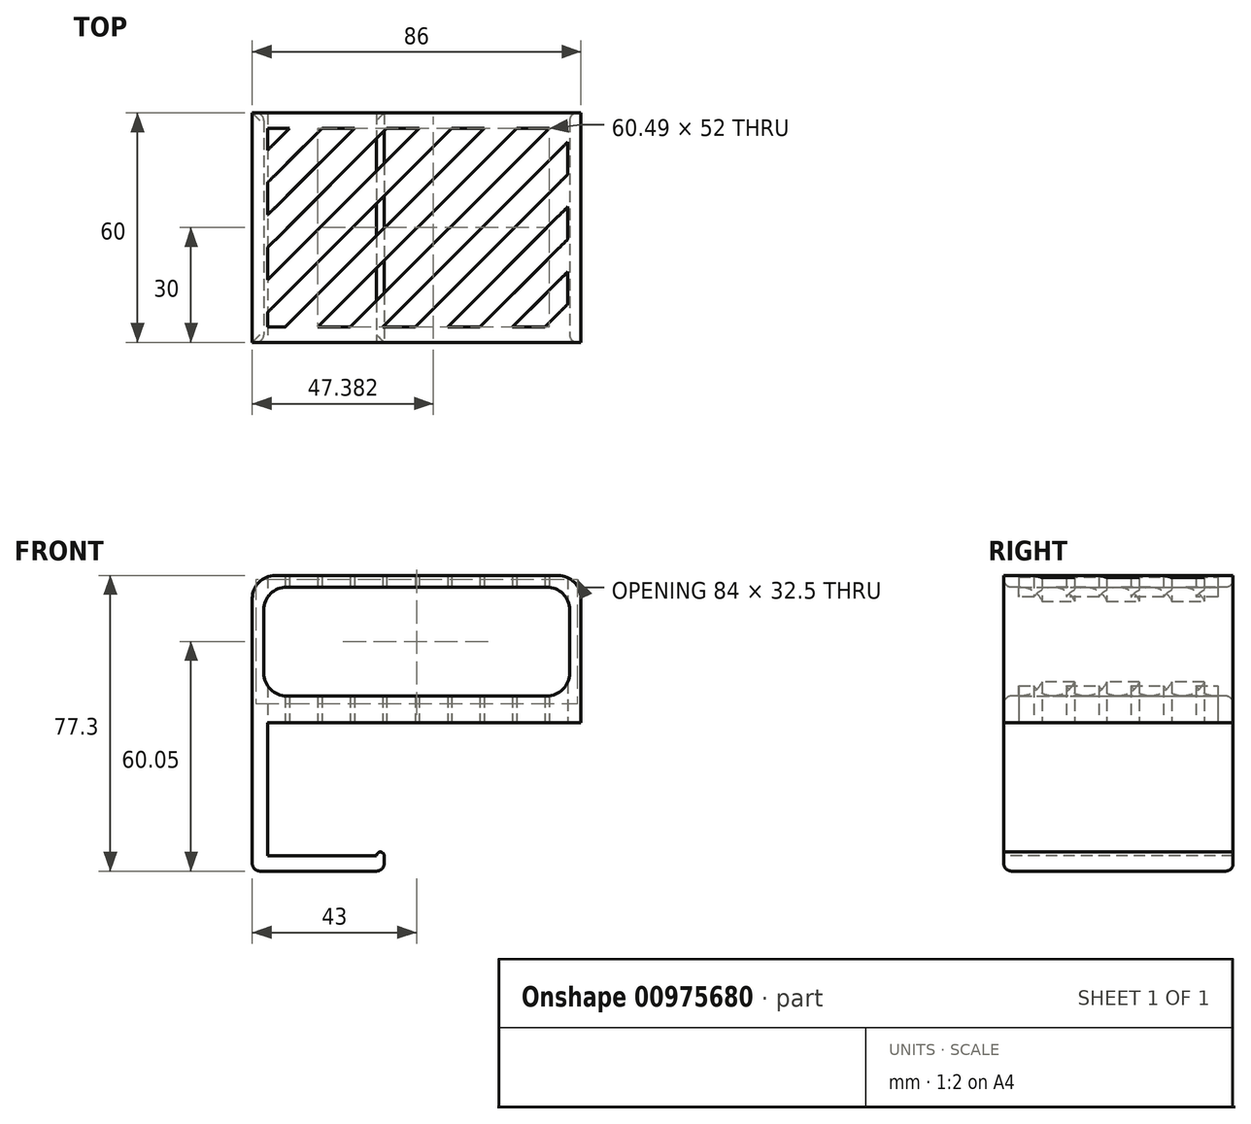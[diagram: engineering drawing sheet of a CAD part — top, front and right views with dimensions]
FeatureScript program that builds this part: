
annotation { "Feature Type Name" : "Feature", "Feature Type Description" : "" }
export const myFeature = defineFeature(function(context is Context, id is Id, definition is map)
    precondition{}
    {
        {
            var Q0;
            Q0=qCreatedBy(makeId("Front.planeOp"),FACE);
            var sketch = newSketch(context, id + "F0", { "sketchPlane" : qUnion([Q0])});
            skLineSegment(sketch, "E0.bottom", {"start": v(0, 51.9) * mm, "end": v(86, 51.9) * mm});
            skLineSegment(sketch, "E0.top", {"start": v(0, 17.4) * mm, "end": v(86, 17.4) * mm});
            skLineSegment(sketch, "E0.left", {"start": v(0, 51.9) * mm, "end": v(0, 17.4) * mm});
            skLineSegment(sketch, "E0.right", {"start": v(86, 51.9) * mm, "end": v(86, 17.4) * mm});
            skLineSegment(sketch, "E1.bottom", {"start": v(3, 48.9) * mm, "end": v(83, 48.9) * mm});
            skLineSegment(sketch, "E1.top", {"start": v(3, 20.4) * mm, "end": v(83, 20.4) * mm});
            skLineSegment(sketch, "E1.left", {"start": v(3, 48.9) * mm, "end": v(3, 20.4) * mm});
            skLineSegment(sketch, "E1.right", {"start": v(83, 48.9) * mm, "end": v(83, 20.4) * mm});
            skSolve(sketch);
        }
        {
            var Q0;
            Q0=qCreatedBy(makeId("Front.planeOp"),FACE);
            var sketch = newSketch(context, id + "F1", { "sketchPlane" : qUnion([Q0])});
            skLineSegment(sketch, "E2", {"start": v(0, 17.4) * mm, "end": v(0, -25.4) * mm});
            skPoint(sketch, "E3.0", {"position": v(86, 17.4) * mm});
            skLineSegment(sketch, "E4", {"start": v(0, 17.4) * mm, "end": v(86, 17.4) * mm});
            skLineSegment(sketch, "E5.0", {"start": v(4, 13.4) * mm, "end": v(86, 13.4) * mm});
            skLineSegment(sketch, "E6.0", {"start": v(0, -25.4) * mm, "end": v(34.5, -25.4) * mm});
            skLineSegment(sketch, "E7", {"start": v(4, -21.4) * mm, "end": v(34.5, -21.4) * mm});
            skLineSegment(sketch, "E8.bottom", {"start": v(34.5, -21.4) * mm, "end": v(32.5, -21.4) * mm});
            skLineSegment(sketch, "E8.top", {"start": v(34.5, -20.4) * mm, "end": v(32.5, -20.4) * mm});
            skLineSegment(sketch, "E8.left", {"start": v(34.5, -21.4) * mm, "end": v(34.5, -20.4) * mm});
            skLineSegment(sketch, "E8.right", {"start": v(32.5, -21.4) * mm, "end": v(32.5, -20.4) * mm});
            skLineSegment(sketch, "E9", {"start": v(63.21, 17.4) * mm, "end": v(-36.45, 17.4) * mm, "construction": true});
            skLineSegment(sketch, "E10", {"start": v(4, -21.4) * mm, "end": v(4, 13.4) * mm});
            skLineSegment(sketch, "E11", {"start": v(86, 13.4) * mm, "end": v(86, 17.4) * mm});
            skLineSegment(sketch, "E12", {"start": v(34.5, -25.4) * mm, "end": v(34.5, -21.4) * mm});
            skLineSegment(sketch, "E13", {"start": v(4, -4) * mm, "end": v(91.63, -4) * mm, "construction": true});
            skSolve(sketch);
        }
        {
            var Q0;
            Q0=makeQuery(id+"F0.imprint","IMPRINT",FACE,{"disambiguationData":[TD([[makeQuery(id+"F0.imprint","IMPRINT",EDGE,{"derivedFrom":sQuery(id+"F0.wireOp",EDGE,"E0.bottom")}),-1.0]])]});
            extrude(context, id + "F2", {"entities" : qUnion([Q0]), "oppositeDirection" : true, "depth" : 60 * mm, "offsetDistance" : 25 * mm});
        }
        {
            var Q0;
            Q0=qSketchRegion(id+"F1",true);
            var Q1;
            Q1=makeQuery(id+"F2.opExtrude","CAP_FACE",FACE,{"disambiguationData":[OSD([sQuery(id+"F0.wireOp",EDGE,"E0.bottom"),sQuery(id+"F0.wireOp",EDGE,"E0.top"),sQuery(id+"F0.wireOp",EDGE,"E0.left"),sQuery(id+"F0.wireOp",EDGE,"E0.right"),sQuery(id+"F0.wireOp",EDGE,"E1.bottom"),sQuery(id+"F0.wireOp",EDGE,"E1.top"),sQuery(id+"F0.wireOp",EDGE,"E1.left"),sQuery(id+"F0.wireOp",EDGE,"E1.right")])],"isStart":false});
            extrude(context, id + "F3", {"entities" : qUnion([Q0]), "operationType" : NewBodyOperationType.ADD, "endBound" : BoundingType.UP_TO_SURFACE, "oppositeDirection" : true, "depth" : 25 * mm, "endBoundEntityFace" : qUnion([Q1]), "offsetDistance" : 25 * mm});
        }
        {
            var Q0;
            Q0=qCreatedBy(makeId("Top.planeOp"),FACE);
            var sketch = newSketch(context, id + "F4", { "sketchPlane" : qUnion([Q0])});
            skLineSegment(sketch, "E14.0", {"start": v(0.04, 0) * mm, "end": v(86.54, 0) * mm, "construction": true});
            skLineSegment(sketch, "E15.0", {"start": v(86.54, 60) * mm, "end": v(86.54, 0) * mm, "construction": true});
            skLineSegment(sketch, "E16.0", {"start": v(86.54, 60) * mm, "end": v(0.04, 60) * mm, "construction": true});
            skLineSegment(sketch, "E17.0", {"start": v(0.04, 60) * mm, "end": v(0.04, 0) * mm, "construction": true});
            skLineSegment(sketch, "E18.0", {"start": v(82.54, 56) * mm, "end": v(82.54, 4) * mm});
            skLineSegment(sketch, "E18.1", {"start": v(82.54, 56) * mm, "end": v(4.04, 56) * mm});
            skLineSegment(sketch, "E18.2", {"start": v(4.04, 56) * mm, "end": v(4.04, 4) * mm});
            skLineSegment(sketch, "E18.3", {"start": v(4.04, 4) * mm, "end": v(82.54, 4) * mm});
            skLineSegment(sketch, "E19", {"start": v(76.54, 4) * mm, "end": v(76.54, 97.18) * mm, "construction": true});
            skLineSegment(sketch, "E20", {"start": v(76.54, 4) * mm, "end": v(82.54, 10) * mm});
            skLineSegment(sketch, "E21.0", {"start": v(68.05, 4) * mm, "end": v(82.54, 18.49) * mm});
            skLineSegment(sketch, "E22.0", {"start": v(59.57, 4) * mm, "end": v(82.54, 26.97) * mm});
            skLineSegment(sketch, "E23.0", {"start": v(51.08, 4) * mm, "end": v(82.54, 35.46) * mm});
            skLineSegment(sketch, "E24.0", {"start": v(42.6, 4) * mm, "end": v(82.54, 43.94) * mm});
            skLineSegment(sketch, "E25.0", {"start": v(34.1, 4) * mm, "end": v(82.54, 52.43) * mm});
            skLineSegment(sketch, "E26.0", {"start": v(25.62, 4) * mm, "end": v(77.62, 56) * mm});
            skLineSegment(sketch, "E27.0", {"start": v(17.14, 4) * mm, "end": v(69.14, 56) * mm});
            skLineSegment(sketch, "E28.0", {"start": v(8.65, 4) * mm, "end": v(60.65, 56) * mm});
            skLineSegment(sketch, "E29.0", {"start": v(4.04, 7.87) * mm, "end": v(52.17, 56) * mm});
            skLineSegment(sketch, "E30.0", {"start": v(5, 60) * mm, "end": v(5, 120) * mm});
            skLineSegment(sketch, "E31.0", {"start": v(4.04, 16.35) * mm, "end": v(43.68, 56) * mm});
            skLineSegment(sketch, "E32.0", {"start": v(4.04, 24.84) * mm, "end": v(35.2, 56) * mm});
            skLineSegment(sketch, "E33.0", {"start": v(4.04, 33.32) * mm, "end": v(26.71, 56) * mm});
            skLineSegment(sketch, "E34.0", {"start": v(4.04, 41.8) * mm, "end": v(18.23, 56) * mm});
            skLineSegment(sketch, "E35.0", {"start": v(4.04, 50.3) * mm, "end": v(9.74, 56) * mm});
            skSolve(sketch);
        }
        {
            var Q0;
            {var subQ0=sQuery(id+"F4.wireOp",EDGE,"E20");Q0=makeQuery(id+"F4.imprint","IMPRINT",FACE,{"disambiguationData":[TD([[makeQuery(id+"F4.imprint","IMPRINT",EDGE,{"derivedFrom":subQ0}),1.0]])]});}
            var Q1;
            {var subQ0=sQuery(id+"F4.wireOp",EDGE,"E22.0");Q1=makeQuery(id+"F4.imprint","IMPRINT",FACE,{"disambiguationData":[TD([[makeQuery(id+"F4.imprint","IMPRINT",EDGE,{"derivedFrom":subQ0}),1.0]])]});}
            var Q2;
            {var subQ0=sQuery(id+"F4.wireOp",EDGE,"E24.0");Q2=makeQuery(id+"F4.imprint","IMPRINT",FACE,{"disambiguationData":[TD([[makeQuery(id+"F4.imprint","IMPRINT",EDGE,{"derivedFrom":subQ0}),1.0]])]});}
            var Q3;
            {var subQ0=sQuery(id+"F4.wireOp",EDGE,"E26.0");var subQ1=sQuery(id+"F4.wireOp",EDGE,"E18.1");var subQ2=makeQuery(id+"F4.imprint","INTERSECT",VERTEX,{"derivedFrom":[subQ1,subQ0]});Q3=makeQuery(id+"F4.imprint","IMPRINT",FACE,{"disambiguationData":[TD([[makeQuery(id+"F4.imprint","IMPRINT",EDGE,{"disambiguationData":[TD([[subQ2,-1.0]])],"derivedFrom":subQ1}),1.0]])]});}
            var Q4;
            {var subQ0=sQuery(id+"F4.wireOp",EDGE,"E26.0");var subQ1=sQuery(id+"F4.wireOp",EDGE,"E18.3");var subQ2=makeQuery(id+"F4.imprint","INTERSECT",VERTEX,{"derivedFrom":[subQ1,subQ0]});Q4=makeQuery(id+"F4.imprint","IMPRINT",FACE,{"disambiguationData":[TD([[makeQuery(id+"F4.imprint","IMPRINT",EDGE,{"disambiguationData":[TD([[subQ2,1.0]])],"derivedFrom":subQ1}),1.0]])]});}
            var Q5;
            {var subQ0=sQuery(id+"F4.wireOp",EDGE,"E28.0");var subQ1=sQuery(id+"F4.wireOp",EDGE,"E18.1");var subQ2=makeQuery(id+"F4.imprint","INTERSECT",VERTEX,{"derivedFrom":[subQ1,subQ0]});Q5=makeQuery(id+"F4.imprint","IMPRINT",FACE,{"disambiguationData":[TD([[makeQuery(id+"F4.imprint","IMPRINT",EDGE,{"disambiguationData":[TD([[subQ2,-1.0]])],"derivedFrom":subQ1}),1.0]])]});}
            var Q6;
            {var subQ1=sQuery(id+"F4.wireOp",EDGE,"E18.2");var subQ6=sQuery(id+"F4.wireOp",EDGE,"E18.3");var subQ9=makeQuery(id+"F4.imprint","INTERSECT",VERTEX,{"derivedFrom":[subQ1,subQ6]});Q6=makeQuery(id+"F4.imprint","IMPRINT",FACE,{"disambiguationData":[TD([[makeQuery(id+"F4.imprint","IMPRINT",EDGE,{"disambiguationData":[TD([[subQ9,1.0]])],"derivedFrom":subQ1}),1.0]])]});}
            var Q7;
            {var subQ0=sQuery(id+"F4.wireOp",EDGE,"E31.0");var subQ1=sQuery(id+"F4.wireOp",EDGE,"E18.2");var subQ2=makeQuery(id+"F4.imprint","INTERSECT",VERTEX,{"derivedFrom":[subQ1,subQ0]});Q7=makeQuery(id+"F4.imprint","IMPRINT",FACE,{"disambiguationData":[TD([[makeQuery(id+"F4.imprint","IMPRINT",EDGE,{"disambiguationData":[TD([[subQ2,1.0]])],"derivedFrom":subQ1}),1.0]])]});}
            var Q8;
            {var subQ0=sQuery(id+"F4.wireOp",EDGE,"E31.0");var subQ1=sQuery(id+"F4.wireOp",EDGE,"E18.1");var subQ2=makeQuery(id+"F4.imprint","INTERSECT",VERTEX,{"derivedFrom":[subQ1,subQ0]});Q8=makeQuery(id+"F4.imprint","IMPRINT",FACE,{"disambiguationData":[TD([[makeQuery(id+"F4.imprint","IMPRINT",EDGE,{"disambiguationData":[TD([[subQ2,-1.0]])],"derivedFrom":subQ1}),1.0]])]});}
            var Q9;
            {var subQ0=sQuery(id+"F4.wireOp",EDGE,"E33.0");Q9=makeQuery(id+"F4.imprint","IMPRINT",FACE,{"disambiguationData":[TD([[makeQuery(id+"F4.imprint","IMPRINT",EDGE,{"derivedFrom":subQ0}),1.0]])]});}
            var Q10;
            {var subQ3=sQuery(id+"F4.wireOp",EDGE,"E35.0");Q10=makeQuery(id+"F4.imprint","IMPRINT",FACE,{"disambiguationData":[TD([[makeQuery(id+"F4.imprint","IMPRINT",EDGE,{"derivedFrom":subQ3}),1.0]])]});}
            var Q11;
            Q11=makeQuery(id+"F2.opExtrude","SWEPT_FACE",FACE,{"disambiguationData":[OSD([sQuery(id+"F0.wireOp",EDGE,"E0.bottom")])]});
            extrude(context, id + "F5", {"entities" : qUnion([Q0, Q1, Q2, Q3, Q4, Q5, Q6, Q7, Q8, Q9, Q10]), "operationType" : NewBodyOperationType.REMOVE, "endBound" : BoundingType.UP_TO_SURFACE, "depth" : 25 * mm, "endBoundEntityFace" : qUnion([Q11]), "offsetDistance" : 25 * mm});
        }
        {
            var Q0;
            Q0=makeQuery(id+"F2.opExtrude","SWEPT_EDGE",EDGE,{"disambiguationData":[OSD([sQuery(id+"F0.wireOp",EDGE,"E1.bottom"),sQuery(id+"F0.wireOp",EDGE,"E1.left")])]});
            var Q1;
            Q1=makeQuery(id+"F2.opExtrude","SWEPT_EDGE",EDGE,{"disambiguationData":[OSD([sQuery(id+"F0.wireOp",EDGE,"E1.top"),sQuery(id+"F0.wireOp",EDGE,"E1.left")])]});
            var Q2;
            Q2=makeQuery(id+"F2.opExtrude","SWEPT_EDGE",EDGE,{"disambiguationData":[OSD([sQuery(id+"F0.wireOp",EDGE,"E1.bottom"),sQuery(id+"F0.wireOp",EDGE,"E1.right")])]});
            var Q3;
            Q3=makeQuery(id+"F2.opExtrude","SWEPT_EDGE",EDGE,{"disambiguationData":[OSD([sQuery(id+"F0.wireOp",EDGE,"E1.top"),sQuery(id+"F0.wireOp",EDGE,"E1.right")])]});
            var Q4;
            Q4=makeQuery(id+"F2.opExtrude","SWEPT_EDGE",EDGE,{"disambiguationData":[OSD([sQuery(id+"F0.wireOp",EDGE,"E0.bottom"),sQuery(id+"F0.wireOp",EDGE,"E0.right")])]});
            var Q5;
            Q5=makeQuery(id+"F2.opExtrude","SWEPT_EDGE",EDGE,{"disambiguationData":[OSD([sQuery(id+"F0.wireOp",EDGE,"E0.top"),sQuery(id+"F0.wireOp",EDGE,"E0.right")])]});
            var Q6;
            Q6=makeQuery(id+"F2.opExtrude","SWEPT_EDGE",EDGE,{"disambiguationData":[OSD([sQuery(id+"F0.wireOp",EDGE,"E0.top"),sQuery(id+"F0.wireOp",EDGE,"E0.left")])]});
            var Q7;
            Q7=makeQuery(id+"F2.opExtrude","SWEPT_EDGE",EDGE,{"disambiguationData":[OSD([sQuery(id+"F0.wireOp",EDGE,"E0.bottom"),sQuery(id+"F0.wireOp",EDGE,"E0.left")])]});
            fillet(context, id + "F6", {"entities" : qUnion([Q0, Q1, Q2, Q3, Q4, Q5, Q6, Q7]), "radius" : 6 * mm, "tangentPropagation" : true, "allowEdgeOverflow" : false});
        }
        {
            var Q0;
            Q0=makeQuery(id+"F2.opExtrude","CAP_EDGE",EDGE,{"disambiguationData":[OSD([sQuery(id+"F0.wireOp",EDGE,"E1.top")])],"isStart":true});
            var Q1;
            Q1=makeQuery(id+"F2.opExtrude","CAP_EDGE",EDGE,{"disambiguationData":[OSD([sQuery(id+"F0.wireOp",EDGE,"E1.top")])],"isStart":false});
            var Q2;
            Q2=makeQuery(id+"F3.opExtrude","SWEPT_EDGE",EDGE,{"disambiguationData":[OSD([sQuery(id+"F1.wireOp",EDGE,"E6.0"),sQuery(id+"F1.wireOp",EDGE,"FEgogpPj-nWPP-g54Q-uAWN-uniVl4YHIuRG")])]});
            var Q3;
            Q3=makeQuery(id+"F3.opExtrude","CAP_EDGE",EDGE,{"disambiguationData":[OSD([sQuery(id+"F1.wireOp",EDGE,"E6.0")])],"isStart":true});
            var Q4;
            Q4=makeQuery(id+"F3.opExtrude","CAP_EDGE",EDGE,{"disambiguationData":[OSD([sQuery(id+"F1.wireOp",EDGE,"E6.0")])],"isStart":false});
            var Q5;
            Q5=makeQuery(id+"F3.opExtrude","SWEPT_EDGE",EDGE,{"disambiguationData":[OSD([sQuery(id+"F1.wireOp",EDGE,"E2"),sQuery(id+"F1.wireOp",EDGE,"E6.0")])]});
            fillet(context, id + "F7", {"entities" : qUnion([Q0, Q1, Q2, Q3, Q4, Q5]), "radius" : 2 * mm, "tangentPropagation" : true, "allowEdgeOverflow" : false});
        }
        {
            var Q0;
            {var subQ0=sQuery(id+"F1.wireOp",EDGE,"916e7058-31fb-4f42-866c-f6f5e89769ae0.MirrorCS");var subQ1=sQuery(id+"F1.wireOp",EDGE,"0a541560-89b6-4e8b-adf3-4228b055bce60.MirrorCS");Q0=makeQuery(id+"F5.boolean.opBoolean","SPLIT",EDGE,{"disambiguationData":[TD([makeQuery(id+"F5.opExtrude","SWEPT_FACE",FACE,{"disambiguationData":[OSD([sQuery(id+"F4.wireOp",EDGE,"E26.0")])]})])],"derivedFrom":makeQuery(id+"F3.opExtrude","SWEPT_EDGE",EDGE,{"disambiguationData":[OSD([subQ1,subQ0])]})});}
            var Q1;
            {var subQ0=sQuery(id+"F1.wireOp",EDGE,"916e7058-31fb-4f42-866c-f6f5e89769ae0.MirrorCS");var subQ1=sQuery(id+"F1.wireOp",EDGE,"aefed43f-0902-40bb-a633-789f5580acaf0.MirrorCS");var subQ2=sQuery(id+"F4.wireOp",EDGE,"E18.3");Q1=makeQuery(id+"F5.boolean.opBoolean","SPLIT",EDGE,{"disambiguationData":[TD([makeQuery(id+"F5.opExtrude","SWEPT_FACE",FACE,{"disambiguationData":[OSD([subQ2]),TDD([makeQuery(id+"F4.imprint","IMPRINT",EDGE,{"disambiguationData":[TD([[makeQuery(id+"F4.imprint","INTERSECT",VERTEX,{"derivedFrom":[subQ2,sQuery(id+"F4.wireOp",EDGE,"E24.0")]}),1.0]])],"derivedFrom":subQ2})])]})])],"derivedFrom":makeQuery(id+"F3.opExtrude","SWEPT_EDGE",EDGE,{"disambiguationData":[OSD([subQ0,subQ1])]})});}
            var Q2;
            {var subQ0=sQuery(id+"F1.wireOp",EDGE,"916e7058-31fb-4f42-866c-f6f5e89769ae0.MirrorCS");var subQ1=sQuery(id+"F1.wireOp",EDGE,"aefed43f-0902-40bb-a633-789f5580acaf0.MirrorCS");Q2=makeQuery(id+"F5.boolean.opBoolean","SPLIT",EDGE,{"disambiguationData":[TD([makeQuery(id+"F5.opExtrude","SWEPT_FACE",FACE,{"disambiguationData":[OSD([sQuery(id+"F4.wireOp",EDGE,"E25.0")])]})])],"derivedFrom":makeQuery(id+"F3.opExtrude","SWEPT_EDGE",EDGE,{"disambiguationData":[OSD([subQ0,subQ1])]})});}
            var Q3;
            {var subQ0=sQuery(id+"F1.wireOp",EDGE,"916e7058-31fb-4f42-866c-f6f5e89769ae0.MirrorCS");var subQ1=sQuery(id+"F1.wireOp",EDGE,"aefed43f-0902-40bb-a633-789f5580acaf0.MirrorCS");Q3=makeQuery(id+"F5.boolean.opBoolean","SPLIT",EDGE,{"disambiguationData":[TD([makeQuery(id+"F5.opExtrude","SWEPT_FACE",FACE,{"disambiguationData":[OSD([sQuery(id+"F4.wireOp",EDGE,"E27.0")])]})])],"derivedFrom":makeQuery(id+"F3.opExtrude","SWEPT_EDGE",EDGE,{"disambiguationData":[OSD([subQ0,subQ1])]})});}
            var Q4;
            {var subQ0=sQuery(id+"F1.wireOp",EDGE,"0a541560-89b6-4e8b-adf3-4228b055bce60.MirrorCS");var subQ1=sQuery(id+"F1.wireOp",EDGE,"916e7058-31fb-4f42-866c-f6f5e89769ae0.MirrorCS");Q4=makeQuery(id+"F5.boolean.opBoolean","SPLIT",EDGE,{"disambiguationData":[TD([makeQuery(id+"F5.opExtrude","SWEPT_FACE",FACE,{"disambiguationData":[OSD([sQuery(id+"F4.wireOp",EDGE,"E27.0")])]})])],"derivedFrom":makeQuery(id+"F3.opExtrude","SWEPT_EDGE",EDGE,{"disambiguationData":[OSD([subQ0,subQ1])]})});}
            var Q5;
            {var subQ0=sQuery(id+"F1.wireOp",EDGE,"0a541560-89b6-4e8b-adf3-4228b055bce60.MirrorCS");var subQ1=sQuery(id+"F1.wireOp",EDGE,"916e7058-31fb-4f42-866c-f6f5e89769ae0.MirrorCS");Q5=makeQuery(id+"F5.boolean.opBoolean","SPLIT",EDGE,{"disambiguationData":[TD([makeQuery(id+"F5.opExtrude","SWEPT_FACE",FACE,{"disambiguationData":[OSD([sQuery(id+"F4.wireOp",EDGE,"E29.0")])]})])],"derivedFrom":makeQuery(id+"F3.opExtrude","SWEPT_EDGE",EDGE,{"disambiguationData":[OSD([subQ0,subQ1])]})});}
            var Q6;
            {var subQ0=sQuery(id+"F1.wireOp",EDGE,"916e7058-31fb-4f42-866c-f6f5e89769ae0.MirrorCS");var subQ1=sQuery(id+"F1.wireOp",EDGE,"aefed43f-0902-40bb-a633-789f5580acaf0.MirrorCS");Q6=makeQuery(id+"F5.boolean.opBoolean","SPLIT",EDGE,{"disambiguationData":[TD([makeQuery(id+"F5.opExtrude","SWEPT_FACE",FACE,{"disambiguationData":[OSD([sQuery(id+"F4.wireOp",EDGE,"E29.0")])]})])],"derivedFrom":makeQuery(id+"F3.opExtrude","SWEPT_EDGE",EDGE,{"disambiguationData":[OSD([subQ0,subQ1])]})});}
            var Q7;
            {var subQ0=sQuery(id+"F1.wireOp",EDGE,"aefed43f-0902-40bb-a633-789f5580acaf0.MirrorCS");var subQ1=sQuery(id+"F1.wireOp",EDGE,"916e7058-31fb-4f42-866c-f6f5e89769ae0.MirrorCS");Q7=makeQuery(id+"F5.boolean.opBoolean","SPLIT",EDGE,{"disambiguationData":[TD([makeQuery(id+"F5.opExtrude","SWEPT_FACE",FACE,{"disambiguationData":[OSD([sQuery(id+"F4.wireOp",EDGE,"E32.0")])]})])],"derivedFrom":makeQuery(id+"F3.opExtrude","SWEPT_EDGE",EDGE,{"disambiguationData":[OSD([subQ1,subQ0])]})});}
            var Q8;
            {var subQ0=sQuery(id+"F1.wireOp",EDGE,"916e7058-31fb-4f42-866c-f6f5e89769ae0.MirrorCS");var subQ1=sQuery(id+"F1.wireOp",EDGE,"0a541560-89b6-4e8b-adf3-4228b055bce60.MirrorCS");Q8=makeQuery(id+"F5.boolean.opBoolean","SPLIT",EDGE,{"disambiguationData":[TD([makeQuery(id+"F5.opExtrude","SWEPT_FACE",FACE,{"disambiguationData":[OSD([sQuery(id+"F4.wireOp",EDGE,"E32.0")])]})])],"derivedFrom":makeQuery(id+"F3.opExtrude","SWEPT_EDGE",EDGE,{"disambiguationData":[OSD([subQ1,subQ0])]})});}
            var Q9;
            Q9=makeQuery(id+"F3.opExtrude","SWEPT_EDGE",EDGE,{"disambiguationData":[OSD([sQuery(id+"F1.wireOp",EDGE,"E8.top"),sQuery(id+"F1.wireOp",EDGE,"E8.left")])]});
            var Q10;
            Q10=makeQuery(id+"F3.opExtrude","SWEPT_EDGE",EDGE,{"disambiguationData":[OSD([sQuery(id+"F1.wireOp",EDGE,"E8.top"),sQuery(id+"F1.wireOp",EDGE,"E8.right")])]});
            var Q11;
            {var subQ0=sQuery(id+"F1.wireOp",EDGE,"b0374f7f-9421-4335-b826-772879a6bbfb0.MirrorCS");var subQ1=sQuery(id+"F1.wireOp",EDGE,"5b5900ed-bd0c-40d9-ae48-3972d69e9b390.MirrorCS");Q11=makeQuery(id+"F5.boolean.opBoolean","SPLIT",EDGE,{"disambiguationData":[TD([makeQuery(id+"F5.opExtrude","SWEPT_FACE",FACE,{"disambiguationData":[OSD([sQuery(id+"F4.wireOp",EDGE,"E32.0")])]})])],"derivedFrom":makeQuery(id+"F3.opExtrude","SWEPT_EDGE",EDGE,{"disambiguationData":[OSD([subQ1,subQ0])]})});}
            var Q12;
            {var subQ0=sQuery(id+"F1.wireOp",EDGE,"b8f30536-bd16-4f78-8444-6fd20c56a3d70.MirrorCS");var subQ1=sQuery(id+"F1.wireOp",EDGE,"b0374f7f-9421-4335-b826-772879a6bbfb0.MirrorCS");Q12=makeQuery(id+"F5.boolean.opBoolean","SPLIT",EDGE,{"disambiguationData":[TD([makeQuery(id+"F5.opExtrude","SWEPT_FACE",FACE,{"disambiguationData":[OSD([sQuery(id+"F4.wireOp",EDGE,"E32.0")])]})])],"derivedFrom":makeQuery(id+"F3.opExtrude","SWEPT_EDGE",EDGE,{"disambiguationData":[OSD([subQ1,subQ0])]})});}
            var Q13;
            {var subQ0=sQuery(id+"F1.wireOp",EDGE,"b0374f7f-9421-4335-b826-772879a6bbfb0.MirrorCS");var subQ1=sQuery(id+"F1.wireOp",EDGE,"b8f30536-bd16-4f78-8444-6fd20c56a3d70.MirrorCS");Q13=makeQuery(id+"F5.boolean.opBoolean","SPLIT",EDGE,{"disambiguationData":[TD([makeQuery(id+"F5.opExtrude","SWEPT_FACE",FACE,{"disambiguationData":[OSD([sQuery(id+"F4.wireOp",EDGE,"E29.0")])]})])],"derivedFrom":makeQuery(id+"F3.opExtrude","SWEPT_EDGE",EDGE,{"disambiguationData":[OSD([subQ0,subQ1])]})});}
            var Q14;
            {var subQ0=sQuery(id+"F1.wireOp",EDGE,"5b5900ed-bd0c-40d9-ae48-3972d69e9b390.MirrorCS");var subQ1=sQuery(id+"F1.wireOp",EDGE,"b0374f7f-9421-4335-b826-772879a6bbfb0.MirrorCS");Q14=makeQuery(id+"F5.boolean.opBoolean","SPLIT",EDGE,{"disambiguationData":[TD([makeQuery(id+"F5.opExtrude","SWEPT_FACE",FACE,{"disambiguationData":[OSD([sQuery(id+"F4.wireOp",EDGE,"E29.0")])]})])],"derivedFrom":makeQuery(id+"F3.opExtrude","SWEPT_EDGE",EDGE,{"disambiguationData":[OSD([subQ0,subQ1])]})});}
            var Q15;
            {var subQ0=sQuery(id+"F1.wireOp",EDGE,"5b5900ed-bd0c-40d9-ae48-3972d69e9b390.MirrorCS");var subQ1=sQuery(id+"F1.wireOp",EDGE,"b0374f7f-9421-4335-b826-772879a6bbfb0.MirrorCS");Q15=makeQuery(id+"F5.boolean.opBoolean","SPLIT",EDGE,{"disambiguationData":[TD([makeQuery(id+"F5.opExtrude","SWEPT_FACE",FACE,{"disambiguationData":[OSD([sQuery(id+"F4.wireOp",EDGE,"E27.0")])]})])],"derivedFrom":makeQuery(id+"F3.opExtrude","SWEPT_EDGE",EDGE,{"disambiguationData":[OSD([subQ0,subQ1])]})});}
            var Q16;
            {var subQ0=sQuery(id+"F1.wireOp",EDGE,"b0374f7f-9421-4335-b826-772879a6bbfb0.MirrorCS");var subQ1=sQuery(id+"F1.wireOp",EDGE,"b8f30536-bd16-4f78-8444-6fd20c56a3d70.MirrorCS");Q16=makeQuery(id+"F5.boolean.opBoolean","SPLIT",EDGE,{"disambiguationData":[TD([makeQuery(id+"F5.opExtrude","SWEPT_FACE",FACE,{"disambiguationData":[OSD([sQuery(id+"F4.wireOp",EDGE,"E27.0")])]})])],"derivedFrom":makeQuery(id+"F3.opExtrude","SWEPT_EDGE",EDGE,{"disambiguationData":[OSD([subQ0,subQ1])]})});}
            var Q17;
            {var subQ0=sQuery(id+"F1.wireOp",EDGE,"b0374f7f-9421-4335-b826-772879a6bbfb0.MirrorCS");var subQ1=sQuery(id+"F1.wireOp",EDGE,"5b5900ed-bd0c-40d9-ae48-3972d69e9b390.MirrorCS");Q17=makeQuery(id+"F5.boolean.opBoolean","SPLIT",EDGE,{"disambiguationData":[TD([makeQuery(id+"F5.opExtrude","SWEPT_FACE",FACE,{"disambiguationData":[OSD([sQuery(id+"F4.wireOp",EDGE,"E26.0")])]})])],"derivedFrom":makeQuery(id+"F3.opExtrude","SWEPT_EDGE",EDGE,{"disambiguationData":[OSD([subQ1,subQ0])]})});}
            var Q18;
            {var subQ0=sQuery(id+"F1.wireOp",EDGE,"b0374f7f-9421-4335-b826-772879a6bbfb0.MirrorCS");var subQ1=sQuery(id+"F1.wireOp",EDGE,"b8f30536-bd16-4f78-8444-6fd20c56a3d70.MirrorCS");Q18=makeQuery(id+"F5.boolean.opBoolean","SPLIT",EDGE,{"disambiguationData":[TD([makeQuery(id+"F5.opExtrude","SWEPT_FACE",FACE,{"disambiguationData":[OSD([sQuery(id+"F4.wireOp",EDGE,"E25.0")])]})])],"derivedFrom":makeQuery(id+"F3.opExtrude","SWEPT_EDGE",EDGE,{"disambiguationData":[OSD([subQ0,subQ1])]})});}
            fillet(context, id + "F8", {"entities" : qUnion([Q0, Q1, Q2, Q3, Q4, Q5, Q6, Q7, Q8, Q9, Q10, Q11, Q12, Q13, Q14, Q15, Q16, Q17, Q18]), "radius" : 1 * mm, "tangentPropagation" : true, "allowEdgeOverflow" : false});
        }
    });
